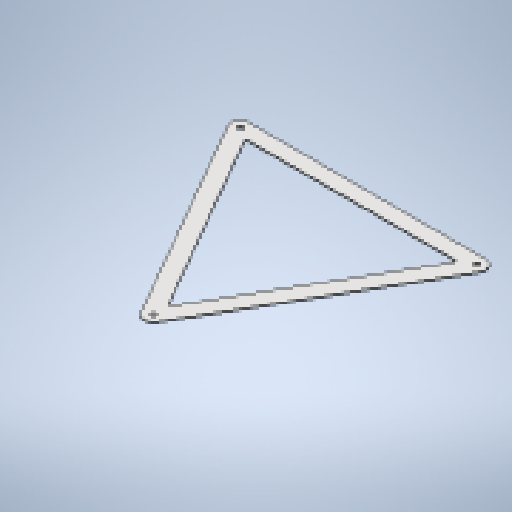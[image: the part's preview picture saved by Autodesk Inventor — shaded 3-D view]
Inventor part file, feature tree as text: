
AUTODESK INVENTOR PART (.ipt)
format: ipt  version: 2025.1 (Build 291241020, 241B)  size: 195,584 bytes
history: native  units: mm
features: other x2, sheet_metal_op x1, chamfer x1, sketch x1
ambient origin geometry x8: Origin, YZ Plane, XZ Plane, XY Plane, X Axis, Y Axis, Z Axis, Center Point
bodies: Solid1 (feature_tree)
feature tree (5):
  sheet_metal_op  "Face1"
  chamfer  "Corner Round3"
  sketch  "Sketch1"  dims[d2=3.0mm d34=17.0mm d35=20.0mm d36=740.47mm d37=740.47mm d38=50.0mm d39=6.0mm]
  other  "Plate1"
  other  "Definition1"
